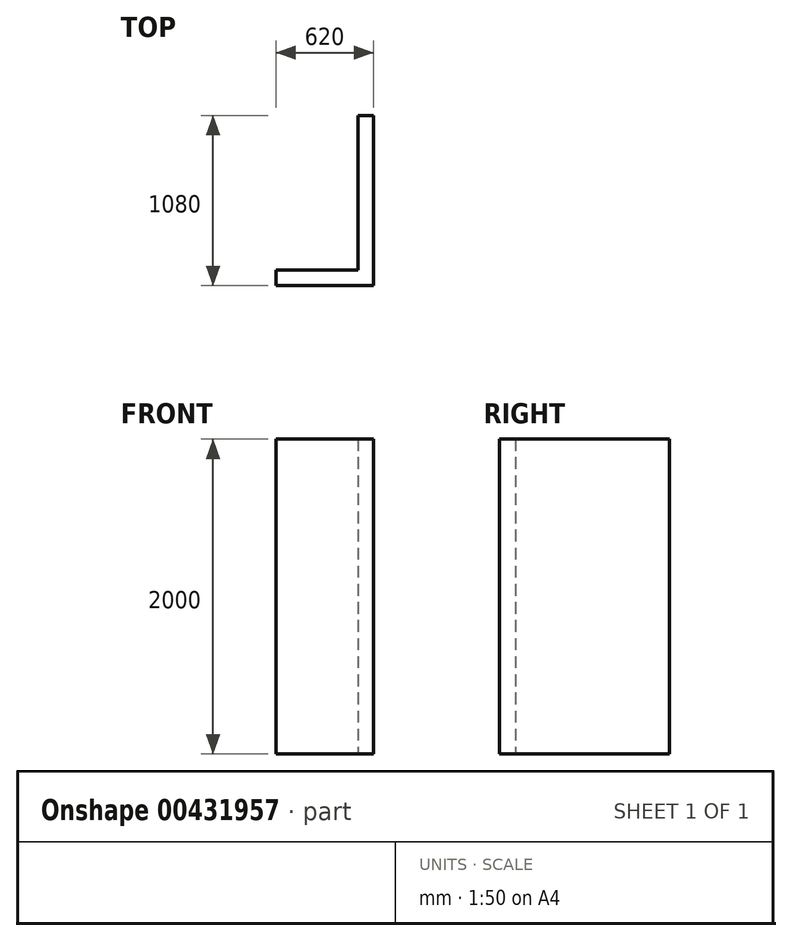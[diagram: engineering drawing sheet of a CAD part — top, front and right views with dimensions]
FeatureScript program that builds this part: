
annotation { "Feature Type Name" : "Feature", "Feature Type Description" : "" }
export const myFeature = defineFeature(function(context is Context, id is Id, definition is map)
    precondition{}
    {
        {
            var Q0;
            Q0=qCreatedBy(makeId("Top.planeOp"),FACE);
            var sketch = newSketch(context, id + "F0", { "sketchPlane" : qUnion([Q0])});
            skLineSegment(sketch, "E0.bottom", {"start": v(50, 540) * mm, "end": v(-50, 540) * mm});
            skLineSegment(sketch, "E0.top", {"start": v(50, -540) * mm, "end": v(-50, -540) * mm});
            skLineSegment(sketch, "E0.left", {"start": v(50, 540) * mm, "end": v(50, -540) * mm});
            skLineSegment(sketch, "E0.right", {"start": v(-50, 540) * mm, "end": v(-50, -540) * mm});
            skPoint(sketch, "E0.middle", {"position": v(0, 0) * mm});
            skLineSegment(sketch, "E1.bottom", {"start": v(-50, -540) * mm, "end": v(-570, -540) * mm});
            skLineSegment(sketch, "E1.top", {"start": v(-50, -440) * mm, "end": v(-570, -440) * mm});
            skLineSegment(sketch, "E1.left", {"start": v(-50, -540) * mm, "end": v(-50, -440) * mm});
            skLineSegment(sketch, "E1.right", {"start": v(-570, -540) * mm, "end": v(-570, -440) * mm});
            skSolve(sketch);
        }
        {
            var Q0;
            Q0 = qSketchRegion(id + "F0", true);
            extrude(context, id + "F1", {"entities" : qUnion([Q0]), "depth" : 2000 * mm});
        }
    });
